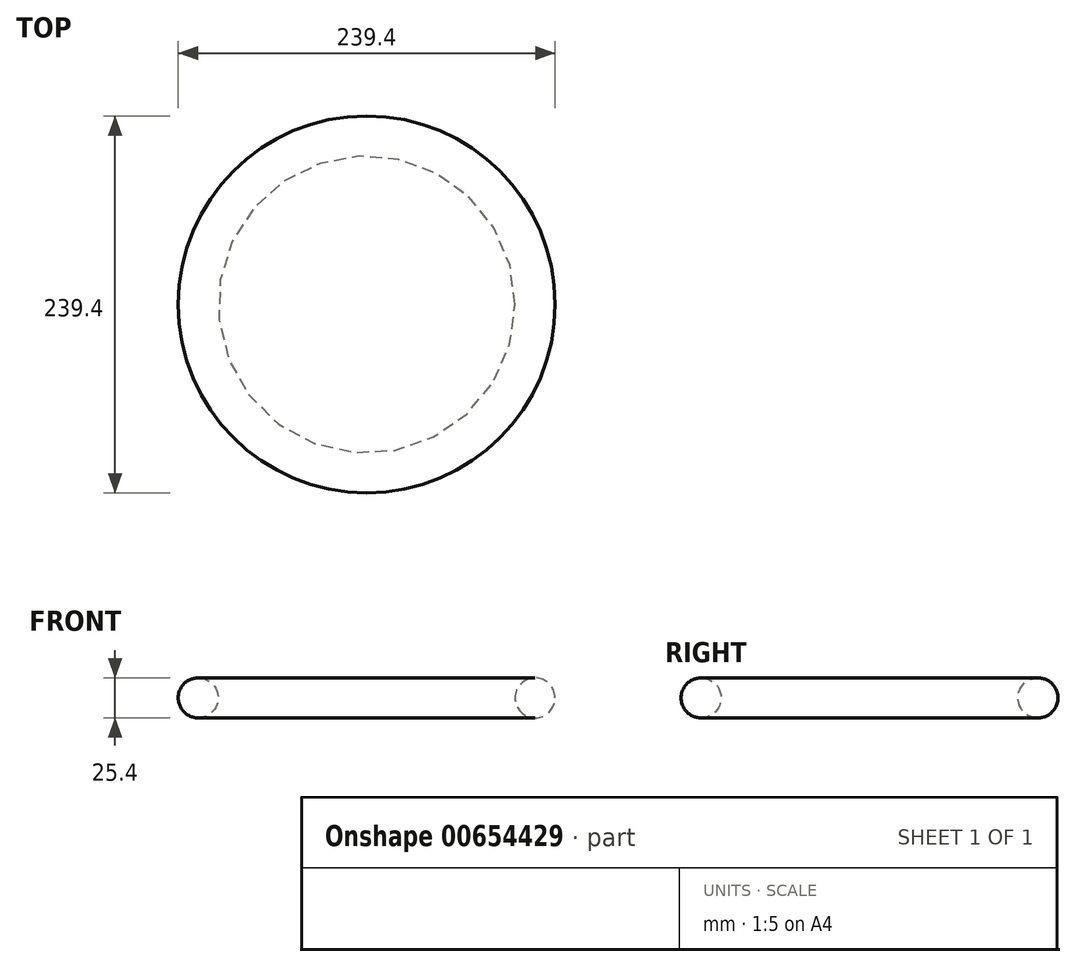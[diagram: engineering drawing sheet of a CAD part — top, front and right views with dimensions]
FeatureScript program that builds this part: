
annotation { "Feature Type Name" : "Feature", "Feature Type Description" : "" }
export const myFeature = defineFeature(function(context is Context, id is Id, definition is map)
    precondition{}
    {
        {
            var Q0;
            Q0=qCreatedBy(makeId("Front.planeOp"),FACE);
            var sketch = newSketch(context, id + "F0", { "sketchPlane" : qUnion([Q0])});
            skCircle(sketch, "E0", {"center": v(107, 0) * mm, "radius": 12.7 * mm});
            skLineSegment(sketch, "E1", {"start": v(0, 0) * mm, "end": v(0, 30.6) * mm});
            skSolve(sketch);
        }
        {
            var Q0;
            Q0=makeQuery(id+"F0.imprint","IMPRINT",FACE,{"disambiguationData":[TD([[makeQuery(id+"F0.imprint","IMPRINT",EDGE,{"derivedFrom":sQuery(id+"F0.wireOp",EDGE,"E0")}),1.0]])]});
            var Q1;
            Q1=sQuery(id+"F0.wireOp",EDGE,"E0");
            var Q2;
            Q2=sQuery(id+"F0.wireOp",EDGE,"E1");
            revolve(context, id + "F1", {"bodyType" : ToolBodyType.SURFACE, "entities" : qUnion([Q0]), "surfaceEntities" : qUnion([Q1]), "axis" : qUnion([Q2]), "revolveType" : RevolveType.FULL});
        }
        {
            var Q0;
            Q0=qCreatedBy(makeId("Right.planeOp"),FACE);
            var sketch = newSketch(context, id + "F2", { "sketchPlane" : qUnion([Q0])});
            skCircle(sketch, "E2", {"center": v(-7.14, 29.78) * mm, "radius": 10.82 * mm});
            skSolve(sketch);
        }
    });
